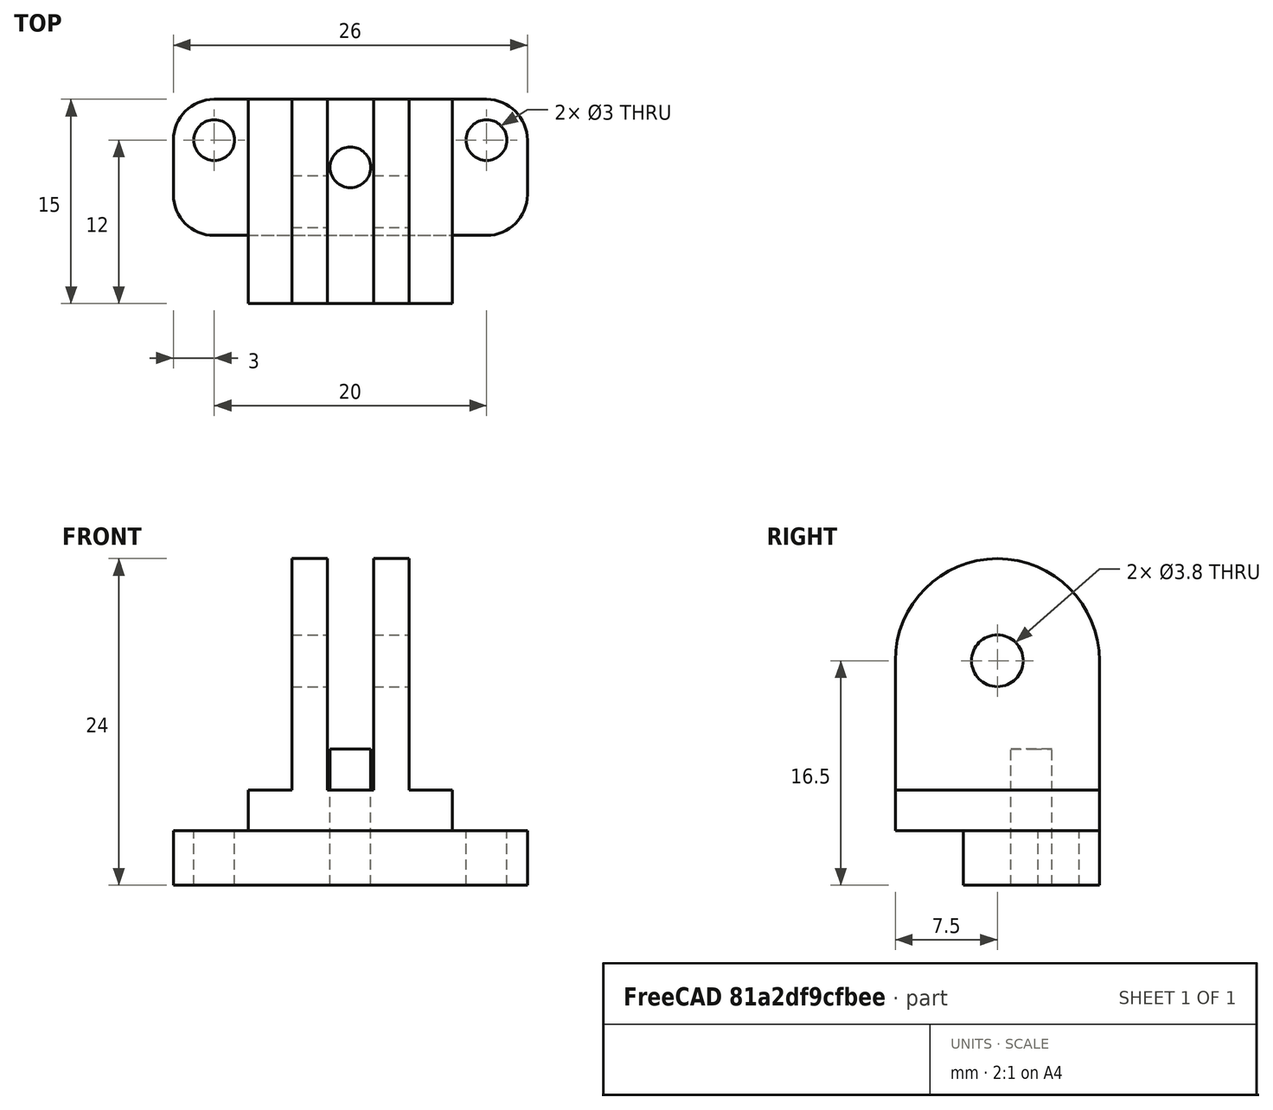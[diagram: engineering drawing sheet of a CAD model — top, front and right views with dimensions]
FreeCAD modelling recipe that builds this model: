
FCSTD DOCUMENT  (FreeCAD 0.19R23578 (Git))
Label: mpu-92_65
License: FreeArt
LicenseURL: http://artlibre.org/licence/lal
objects: Part::Box×1, Spreadsheet::Sheet×1, Part::Feature×1, Part::Cylinder×1, Part::FeaturePython×1, Part::Fillet×1, Part::MultiFuse×1, Part::Cut×1, App::Part×1
note: 6 computed .brp shape members not serialized (recipe doc carries the construction recipe); baked Part::Feature solids carry a one-line shape summary decoded from their .brp

FEATURE [Part::Box] Box008  label="sensor holder cube"
  AttacherType = Attacher::AttachEngine3D
  Height = 4
  Length = 26
  Placement = pos=(-13,-2.5,0) rot=(0,0,1;0rad)
  Width = 10
  expr: Length = <<p>>.sensor_holder_x
  expr: Height = <<p>>.sensor_holder_z
  expr: Width = <<p>>.sensor_holder_y
  expr: .Placement.Base.x = -<<p>>.sensor_holder_x / 2
  expr: .Placement.Base.y = 15 / 2 - <<p>>.sensor_holder_y
FEATURE [Spreadsheet::Sheet] Spreadsheet001  label="p"
  cells = A1=sensor_holder_x; B1(sensor_holder_x)=26; A2=sensor_holder_y; B2(sensor_holder_y)=10; A3=sensor_holder_z; B3(sensor_holder_z)=4; A4=hole_dist_x; B4(hole_dist_x)=20; A5=hole_off_y; B5(hole_off_y)=3; A6=hole_r; B6(hole_r)=1.5
FEATURE [Part::Feature] Cut001001  label="side 2 cut"
  Placement = pos=(0,0,4) rot=(0,0,1;1.5708rad)
  shape: bbox 15 x 15 x 20 mm, 16 faces (baked)
  expr: .Placement.Base.z = <<p>>.sensor_holder_z
FEATURE [Part::Cylinder] Cylinder001  label="screw hole"
  Angle = 360
  AttacherType = Attacher::AttachEngine3D
  Height = 10
  Placement = pos=(0,2.5,0) rot=(0,0,1;0rad)
  Radius = 1.5
  expr: Radius = <<p>>.hole_r
  expr: .Placement.Base.y = <<p>>.sensor_holder_y - 15 / 2
FEATURE [Part::FeaturePython] Array  label="screw hole array"  # Draft array (typed FeaturePython)
  Angle = 360
  ArrayType = 0
  Axis = (0,0,1)
  Base = -> Cylinder001
  Center = (0,0,0)
  Count = 2
  ExpandArray = false
  Fuse = false
  IntervalAxis = (0,0,0)
  IntervalX = (20,0,0)
  IntervalY = (0,100,0)
  IntervalZ = (0,0,100)
  NumberCircles = 3
  NumberPolar = 5
  NumberX = 2
  NumberY = 1
  NumberZ = 1
  Placement = pos=(-10,2,0) rot=(0,0,1;0rad)
  PlacementList = 2 placements: [(0,2.5,0),(20,2.5,0)]
  RadialDistance = 50
  ScaleList = (2) [(1,1,1),(1,1,1)]
  Symmetry = 1
  TangentialDistance = 25
  expr: .Placement.Base.y = <<p>>.sensor_holder_y / 2 - <<p>>.hole_off_y
  expr: .IntervalX.x = <<p>>.hole_dist_x
  expr: .Placement.Base.x = -<<p>>.hole_dist_x / 2
FEATURE [Part::Fillet] Fillet  label="sensor holder fillet"
  Base = -> Box008
  Edges = 4 edges r=3: [Edge1,Edge3,Edge5,Edge7]
FEATURE [Part::MultiFuse] Fusion  label="body fusion"
  Shapes = -> [Cut001001,Fillet]
FEATURE [Part::Cut] Cut001002  label="body cut"
  Base = -> Fusion
  Tool = -> Array
FEATURE [App::Part] Part  label="pcb box part"
  Group = -> [Cut001001,Fusion,Cut001002]
  Origin = -> Origin
